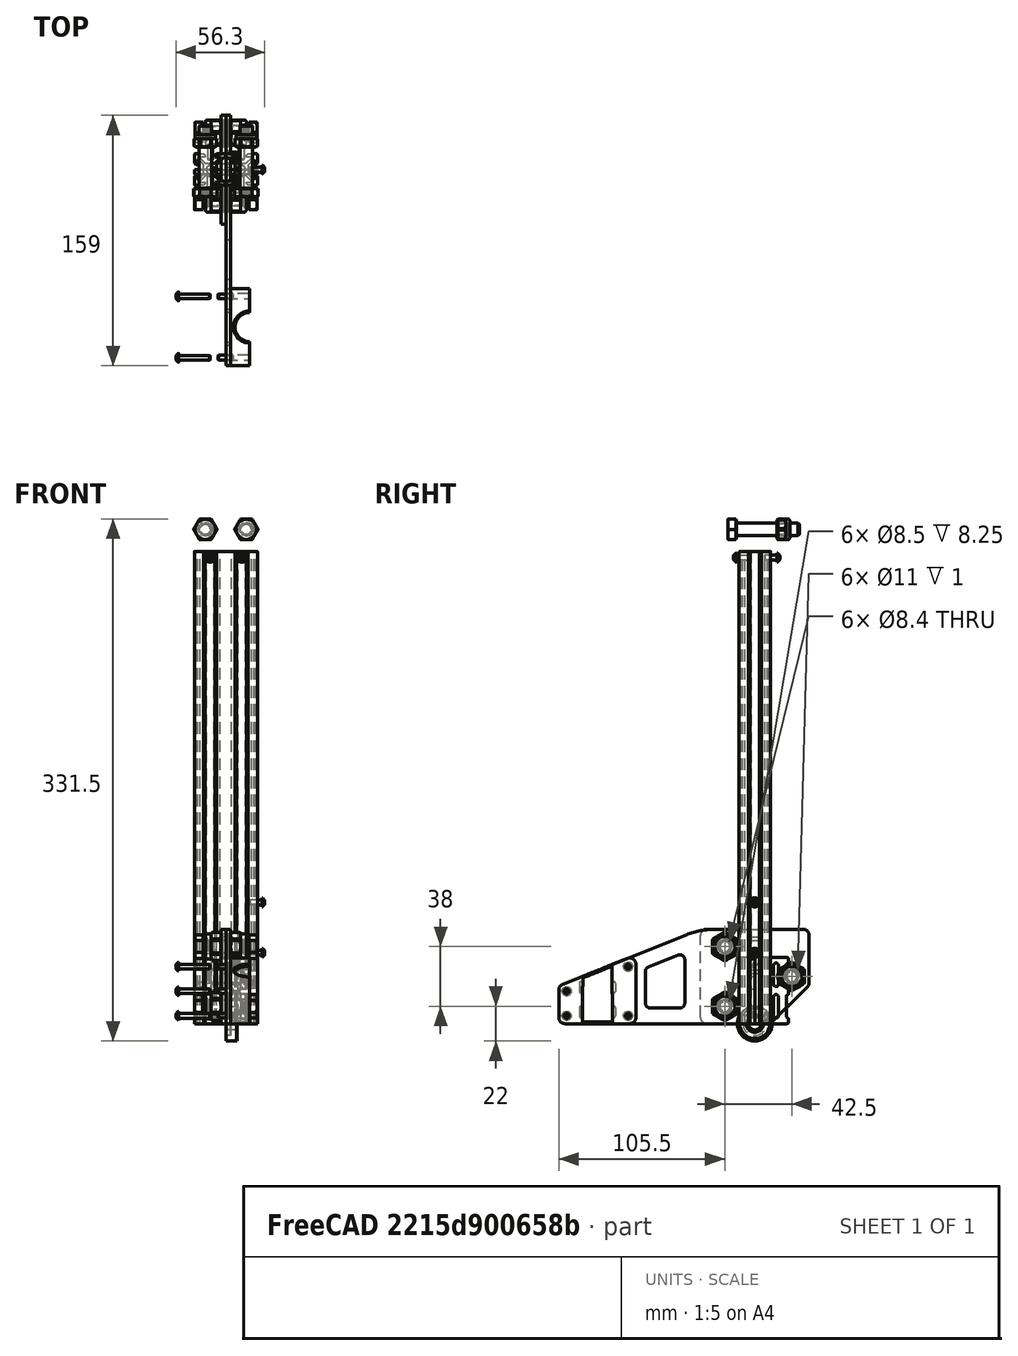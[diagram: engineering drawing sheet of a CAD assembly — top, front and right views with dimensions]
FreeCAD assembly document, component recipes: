
FREECAD ASSEMBLY — COMPONENT RECIPES ("BarbaHeatSetInsertPress")

This assembly document has 10 components, labeled P0..P9 below (a component is one placed body or linked part). 9 of them carry a construction recipe — the FreeCAD feature program that regenerates the part from scratch, quoted from this document or its linked companion documents; the rest are supplied as boundary geometry only. No exploded tour is included for this assembly.
COMPONENT P0 — recipe-attached ("PorteFer", modeled in this document).
Construction recipe (the document's own serialized feature program — sketch geometry with constraints, then the solid features built on it; lengths are millimeters unless a unit is written):

FEATURE [Sketcher::SketchObject] Sketch
  FullyConstrained = true
  MapMode = 5
  Placement = pos=(0,0,0) rot=(0.57735,0.57735,0.57735;2.0944rad)
  Support = -> [YZ_Plane]
  sketch-geometry (53):
    g0: LineSegment StartX=-124.5 StartY=0 StartZ=0 EndX=-124.5 EndY=24 EndZ=0
    g1: LineSegment StartX=-124.5 StartY=24 StartZ=0 EndX=-34.5 EndY=60 EndZ=0
    g2: LineSegment StartX=-34.5 StartY=60 StartZ=0 EndX=34.5 EndY=60 EndZ=0
    g3: LineSegment StartX=34.5 StartY=60 StartZ=0 EndX=34.5 EndY=24.5 EndZ=0
    g4: LineSegment StartX=34.5 StartY=24.5 StartZ=0 EndX=10 EndY=0 EndZ=0
    g5: LineSegment StartX=10 StartY=0 StartZ=0 EndX=-124.5 EndY=0 EndZ=0
    g6: LineSegment [constr] StartX=-109.5 StartY=0 StartZ=0 EndX=-109.5 EndY=30 EndZ=0
    g7: LineSegment [constr] StartX=-90.5 StartY=37.6 StartZ=0 EndX=-90.5 EndY=0 EndZ=0
    g8: LineSegment [constr] StartX=-100 StartY=0 StartZ=0 EndX=-100 EndY=33.8 EndZ=0
    g9: LineSegment [constr] StartX=10 StartY=0 StartZ=0 EndX=10 EndY=60 EndZ=0
    g10: LineSegment [constr] StartX=-10 StartY=60 StartZ=0 EndX=-10 EndY=0 EndZ=0
    g11: Circle [constr] CenterX=-19 CenterY=49 CenterZ=0 NormalX=0 NormalY=0 NormalZ=1 AngleXU=0 Radius=11
    g12: Circle [constr] CenterX=-19 CenterY=11 CenterZ=0 NormalX=0 NormalY=0 NormalZ=1 AngleXU=0 Radius=11
    g13: Circle CenterX=-19 CenterY=49 CenterZ=0 NormalX=0 NormalY=0 NormalZ=1 AngleXU=0 Radius=4.05
    g14: Circle CenterX=-19 CenterY=11 CenterZ=0 NormalX=0 NormalY=0 NormalZ=1 AngleXU=0 Radius=4.05
    g15: LineSegment [constr] StartX=-19 StartY=49 StartZ=0 EndX=-19 EndY=11 EndZ=0
    g16: LineSegment [constr] StartX=-19 StartY=30 StartZ=0 EndX=18.5 EndY=30 EndZ=0
    g17: ArcOfCircle CenterX=18.5 CenterY=30 CenterZ=0 NormalX=0 NormalY=0 NormalZ=1 AngleXU=0 Radius=4.05 StartAngle=1.5708 EndAngle=4.71239
    g18: ArcOfCircle CenterX=23.5 CenterY=30 CenterZ=0 NormalX=0 NormalY=0 NormalZ=1 AngleXU=0 Radius=4.05 StartAngle=4.71239 EndAngle=7.85398
    g19: LineSegment StartX=18.5 StartY=25.95 StartZ=0 EndX=23.5 EndY=25.95 EndZ=0
    g20: LineSegment StartX=18.5 StartY=34.05 StartZ=0 EndX=23.5 EndY=34.05 EndZ=0
    g21: LineSegment StartX=-69.5 StartY=10 StartZ=0 EndX=-69.5 EndY=35.2297 EndZ=0
    g22: LineSegment StartX=-69.5 StartY=35.2297 StartZ=0 EndX=-44.5 EndY=45.2297 EndZ=0
    g23: LineSegment StartX=-44.5 StartY=45.2297 StartZ=0 EndX=-44.5 EndY=10 EndZ=0
    g24: LineSegment StartX=-44.5 StartY=10 StartZ=0 EndX=-69.5 EndY=10 EndZ=0
    g25: Circle CenterX=-119.5 CenterY=20.6148 CenterZ=0 NormalX=0 NormalY=0 NormalZ=1 AngleXU=0 Radius=1.6
    g26: Circle CenterX=-119.5 CenterY=5 CenterZ=0 NormalX=0 NormalY=0 NormalZ=1 AngleXU=0 Radius=1.6
    g27: Circle CenterX=-80.5 CenterY=36.2148 CenterZ=0 NormalX=0 NormalY=0 NormalZ=1 AngleXU=0 Radius=1.6
    g28: Circle CenterX=-80.5 CenterY=5 CenterZ=0 NormalX=0 NormalY=0 NormalZ=1 AngleXU=0 Radius=1.6
    g29: ArcOfCircle CenterX=-110.5 CenterY=25.6148 CenterZ=0 NormalX=0 NormalY=0 NormalZ=1 AngleXU=0 Radius=1 StartAngle=1.9e-15 EndAngle=3.14159
    g30: ArcOfCircle CenterX=-110.5 CenterY=20.6148 CenterZ=0 NormalX=0 NormalY=0 NormalZ=1 AngleXU=0 Radius=1 StartAngle=3.14159 EndAngle=6.28319
    g31: LineSegment StartX=-111.5 StartY=25.6148 StartZ=0 EndX=-111.5 EndY=20.6148 EndZ=0
    g32: LineSegment StartX=-109.5 StartY=25.6148 StartZ=0 EndX=-109.5 EndY=20.6148 EndZ=0
    g33: ArcOfCircle CenterX=-110.5 CenterY=10 CenterZ=0 NormalX=0 NormalY=0 NormalZ=1 AngleXU=0 Radius=1 StartAngle=-9e-16 EndAngle=3.14159
    g34: ArcOfCircle CenterX=-110.5 CenterY=5 CenterZ=0 NormalX=0 NormalY=0 NormalZ=1 AngleXU=0 Radius=1 StartAngle=3.14159 EndAngle=6.28319
    g35: LineSegment StartX=-111.5 StartY=10 StartZ=0 EndX=-111.5 EndY=5 EndZ=0
    g36: LineSegment StartX=-109.5 StartY=10 StartZ=0 EndX=-109.5 EndY=5 EndZ=0
    g37: ArcOfCircle CenterX=-89.5 CenterY=25.6148 CenterZ=0 NormalX=0 NormalY=0 NormalZ=1 AngleXU=0 Radius=1 StartAngle=1e-15 EndAngle=3.14159
    g38: ArcOfCircle CenterX=-89.5 CenterY=20.6148 CenterZ=0 NormalX=0 NormalY=0 NormalZ=1 AngleXU=0 Radius=1 StartAngle=3.14159 EndAngle=6.28319
    g39: LineSegment StartX=-90.5 StartY=25.6148 StartZ=0 EndX=-90.5 EndY=20.6148 EndZ=0
    g40: LineSegment StartX=-88.5 StartY=25.6148 StartZ=0 EndX=-88.5 EndY=20.6148 EndZ=0
    g41: ArcOfCircle CenterX=-89.5 CenterY=10 CenterZ=0 NormalX=0 NormalY=0 NormalZ=1 AngleXU=0 Radius=1 StartAngle=-9e-16 EndAngle=3.14159
    g42: ArcOfCircle CenterX=-89.5 CenterY=5 CenterZ=0 NormalX=0 NormalY=0 NormalZ=1 AngleXU=0 Radius=1 StartAngle=3.14159 EndAngle=6.28319
    g43: LineSegment StartX=-90.5 StartY=10 StartZ=0 EndX=-90.5 EndY=5 EndZ=0
    g44: LineSegment StartX=-88.5 StartY=10 StartZ=0 EndX=-88.5 EndY=5 EndZ=0
    g45: LineSegment StartX=-3.5 StartY=55 StartZ=0 EndX=3.5 EndY=55 EndZ=0
    g46: LineSegment StartX=3.5 StartY=55 StartZ=0 EndX=3.5 EndY=52.5 EndZ=0
    g47: LineSegment StartX=3.5 StartY=52.5 StartZ=0 EndX=-3.5 EndY=52.5 EndZ=0
    g48: LineSegment StartX=-3.5 StartY=52.5 StartZ=0 EndX=-3.5 EndY=55 EndZ=0
    g49: LineSegment StartX=-3.5 StartY=44.5 StartZ=0 EndX=3.5 EndY=44.5 EndZ=0
    g50: LineSegment StartX=3.5 StartY=44.5 StartZ=0 EndX=3.5 EndY=42 EndZ=0
    g51: LineSegment StartX=3.5 StartY=42 StartZ=0 EndX=-3.5 EndY=42 EndZ=0
    g52: LineSegment StartX=-3.5 StartY=42 StartZ=0 EndX=-3.5 EndY=44.5 EndZ=0
  constraints (143):
    c: PointOnObject(g0,g-1)
    c: Vertical(g0)
    c: Coincident(g0,g1)
    c: Coincident(g1,g2)
    c: Coincident(g2,g3)
    c: Vertical(g3)
    c: Coincident(g3,g4)
    c: PointOnObject(g4,g-1)
    c: Coincident(g4,g5)
    c: Coincident(g5,g0)
    c: DistanceX(g-1,g4) = 10
    c: PointOnObject(g6,g5)
    c: PointOnObject(g6,g1)
    c: Vertical(g6)
    c: PointOnObject(g7,g1)
    c: PointOnObject(g7,g5)
    c: Vertical(g7)
    c: DistanceX(g6,g7) = 19
    c: PointOnObject(g8,g1)
    c: Vertical(g8)
    c: Symmetric(g6,g7,g8)
    c: DistanceX(g8,g-1) = 100
    c: DistanceX(g0,g6) = 15
    c: Symmetric(g2,g1,g-2)
    c: Angle(g4,g5) = 2.35619
    c: Coincident(g9,g4)
    c: PointOnObject(g9,g2)
    c: Vertical(g9)
    c: PointOnObject(g10,g5)
    c: Vertical(g10)
    c: Symmetric(g10,g9,g-2)
    c: Diameter(g11) = 22
    c: Equal(g11,g12)
    c: DistanceX(g11,g10) = 9
    c: Vertical(g12,g11)
    c: Coincident(g13,g11)
    c: Coincident(g14,g12)
    c: Diameter(g13) = 8.1
    c: Equal(g13,g14)
    c: Coincident(g15,g13)
    c: Coincident(g15,g14)
    c: Symmetric(g14,g13,g16)
    c: DistanceX(g9,g16) = 8.5
    c: Tangent(g17,g20) = 1.5708
    c: Tangent(g17,g19) = -1.5708
    c: Tangent(g19,g18) = -1.5708
    c: Tangent(g20,g18) = 1.5708
    c: Horizontal(g19)
    c: Equal(g17,g18)
    c: Coincident(g17,g16)
    c: Equal(g17,g13)
    c: DistanceX(g17,g18) = 5
    c: DistanceY(g13,g10) = 11
    c: Symmetric(g10,g10,g16)
    c: DistanceX(g18,g3) = 11
    c: DistanceY(g6,g6) = 30
    c: DistanceY(g1) = 60
    c: Vertical(g21)
    c: Coincident(g21,g22)
    c: Coincident(g22,g23)
    c: Vertical(g23)
    c: Coincident(g23,g24)
    c: Coincident(g24,g21)
    c: Horizontal(g24)
    c: DistanceY(g23) = 10
    c: Parallel(g22,g1)
    c: Distance(g22,g1) = 10
    c: DistanceX(g22,g1) = 10
    c: DistanceX(g24,g24) = 25
    c: Equal(g25,g26)
    c: Equal(g26,g27)
    c: Equal(g27,g28)
    c: Diameter(g27) = 3.2
    c: Vertical(g26,g25)
    c: Vertical(g28,g27)
    c: DistanceX(g0,g25) = 5
    c: DistanceY(g0,g26) = 5
    c: Distance(g25,g1) = 5
    c: Distance(g27,g1) = 5
    c: Symmetric(g26,g28,g8)
    c: Tangent(g29,g32) = 1.5708
    c: Tangent(g29,g31) = -1.5708
    c: Tangent(g31,g30) = -1.5708
    c: Tangent(g32,g30) = 1.5708
    c: Vertical(g31)
    c: Equal(g29,g30)
    c: Tangent(g33,g36) = 1.5708
    c: Tangent(g33,g35) = -1.5708
    c: Tangent(g35,g34) = -1.5708
    c: Tangent(g36,g34) = 1.5708
    c: Vertical(g35)
    c: Equal(g33,g34)
    c: Tangent(g37,g40) = 1.5708
    c: Tangent(g37,g39) = -1.5708
    c: Tangent(g39,g38) = -1.5708
    c: Tangent(g40,g38) = 1.5708
    c: Vertical(g39)
    c: Equal(g37,g38)
    c: Tangent(g41,g44) = 1.5708
    c: Tangent(g41,g43) = -1.5708
    c: Tangent(g43,g42) = -1.5708
    c: Tangent(g44,g42) = 1.5708
    c: Vertical(g43)
    c: Equal(g41,g42)
    c: Horizontal(g34,g42)
    c: Horizontal(g29,g37)
    c: Equal(g30,g38)
    c: Equal(g38,g41)
    c: Equal(g41,g33)
    c: PointOnObject(g41,g7)
    c: PointOnObject(g37,g7)
    c: PointOnObject(g29,g6)
    c: PointOnObject(g33,g6)
    c: Equal(g36,g32)
    c: Equal(g32,g39)
    c: Equal(g39,g43)
    c: DistanceY(g30,g29) = 5
    c: Horizontal(g34,g26)
    c: Horizontal(g30,g25)
    c: Diameter(g29) = 2
    c: Coincident(g45,g46)
    c: Coincident(g46,g47)
    c: Coincident(g47,g48)
    c: Coincident(g48,g45)
    c: Horizontal(g45)
    c: Horizontal(g47)
    c: Vertical(g46)
    c: Vertical(g48)
    c: Coincident(g49,g50)
    c: Coincident(g50,g51)
    c: Coincident(g51,g52)
    c: Coincident(g52,g49)
    c: Horizontal(g51)
    c: Vertical(g50)
    c: Vertical(g52)
    c: Symmetric(g49,g49,g-2)
    c: Vertical(g49,g46)
    c: Equal(g50,g46)
    c: DistanceX(g45,g45) = 7
    c: Vertical(g49,g47)
    c: DistanceY(g46,g46) = 2.5
    c: DistanceY(g45,g2) = 5
    c: DistanceY(g49,g46) = 8
FEATURE [PartDesign::Pad] Pad
  AddSubType = 0
  CheckUpToFaceLimits = true
  ClaimChildren = false
  Direction = (1,1,1)
  Fit = 0
  FitJoin = 0
  InnerFit = 0
  InnerFitJoin = 0
  InnerTaperAngle = 0
  InnerTaperAngleRev = 0
  Length = 3
  Length2 = 100
  Linearize = true
  NewSolid = false
  Placement = pos=(0,0,0) rot=(0.57735,0.57735,0.57735;2.0944rad)
  Profile = -> Sketch
  Refine = true
  Suppress = false
  Type = 0
  _ProfileBasedVersion = 1
FEATURE [PartDesign::Fillet] Fillet
  AddSubType = 0
  Base = -> Pad [Edge8,Edge2,Edge1]
  BaseFeature = -> Pad
  NewSolid = false
  Placement = pos=(0,0,0) rot=(0.57735,0.57735,0.57735;2.0944rad)
  Radius = 4
  Refine = true
  SupportTransform = false
  Suppress = false
FEATURE [PartDesign::Fillet] Fillet001
  AddSubType = 0
  Base = -> Fillet [Edge101,Edge99]
  BaseFeature = -> Fillet
  NewSolid = false
  Placement = pos=(0,0,0) rot=(0.57735,0.57735,0.57735;2.0944rad)
  Radius = 3
  Refine = true
  SupportTransform = false
  Suppress = false
FEATURE [PartDesign::Fillet] Fillet002
  AddSubType = 0
  Base = -> Fillet001 [Edge67]
  BaseFeature = -> Fillet001
  NewSolid = false
  Placement = pos=(0,0,0) rot=(0.57735,0.57735,0.57735;2.0944rad)
  Radius = 50
  Refine = true
  SupportTransform = false
  Suppress = false
FEATURE [PartDesign::Fillet] Fillet003
  AddSubType = 0
  Base = -> Fillet002 [Edge78,Edge80,Edge75,Edge76]
  BaseFeature = -> Fillet002
  NewSolid = false
  Placement = pos=(0,0,0) rot=(0.57735,0.57735,0.57735;2.0944rad)
  Radius = 3
  Refine = true
  SupportTransform = false
  Suppress = false
FEATURE [PartDesign::Body] Body  label="PorteFer"
  AutoGroupSolids = false
  ExportMode = 0
  Group = -> [Sketch,Pad,Fillet,Fillet001,Fillet002,Fillet003]
  Origin = -> Origin
  SingleSolid = true
  Tip = -> Fillet003
  _ExportChildren = -> [Pad,Fillet,Fillet001,Fillet002,Fillet003]
  _GroupVersion = 1
COMPONENT P1 — recipe-attached ("Rondelle", modeled in this document).
Construction recipe (the document's own serialized feature program — sketch geometry with constraints, then the solid features built on it; lengths are millimeters unless a unit is written):

FEATURE [Sketcher::SketchObject] Sketch001
  FullyConstrained = true
  MapMode = 5
  Placement = pos=(0,0,0) rot=(0.57735,0.57735,0.57735;2.0944rad)
  Support = -> [YZ_Plane001]
  sketch-geometry (2):
    g0: Circle CenterX=0 CenterY=0 CenterZ=0 NormalX=0 NormalY=0 NormalZ=1 AngleXU=0 Radius=4
    g1: Circle CenterX=0 CenterY=0 CenterZ=0 NormalX=0 NormalY=0 NormalZ=1 AngleXU=0 Radius=7.5
  constraints (4):
    c: Coincident(g0,g-1)
    c: Coincident(g1,g0)
    c: Diameter(g0) = 8
    c: Diameter(g1) = 15
FEATURE [PartDesign::Pad] Pad001
  AddSubType = 0
  CheckUpToFaceLimits = true
  ClaimChildren = false
  Direction = (1,1,1)
  Fit = 0
  FitJoin = 0
  InnerFit = 0
  InnerFitJoin = 0
  InnerTaperAngle = 0
  InnerTaperAngleRev = 0
  Length = 3
  Length2 = 100
  Linearize = true
  NewSolid = false
  Placement = pos=(0,0,0) rot=(0.57735,0.57735,0.57735;2.0944rad)
  Profile = -> Sketch001
  Refine = true
  Suppress = false
  Type = 0
  _ProfileBasedVersion = 1
FEATURE [PartDesign::Body] Body001  label="Rondelle"
  AutoGroupSolids = false
  ExportMode = 0
  Group = -> [Sketch001,Pad001]
  Origin = -> Origin001
  SingleSolid = true
  Tip = -> Pad001
  _ExportChildren = -> [Pad001]
  _GroupVersion = 1
COMPONENT P2 — recipe-attached ("Chariot", modeled in this document).
Construction recipe (the document's own serialized feature program — sketch geometry with constraints, then the solid features built on it; lengths are millimeters unless a unit is written):

FEATURE [PartDesign::SubShapeBinder] Binder  label="Binder(Fillet003)"
  BindCopyOnChange = 0
  BindMode = 0
  ClaimChildren = false
  Context = -> Body002 [Binder.]
  FillStyle = 0
  Fuse = false
  MakeFace = true
  PartialLoad = false
  Relative = true
  Support = -> [Body[Fillet003.Face1]]
  _Version = 8
FEATURE [Sketcher::SketchObject] Sketch002
  ExternalGeometry = -> [Binder]
  FullyConstrained = true
  MapMode = 5
  Placement = pos=(0,0,0) rot=(0.57735,0.57735,0.57735;2.0944rad)
  Support = -> [YZ_Plane002]
  sketch-geometry (8):
    g0: LineSegment StartX=8.75736 StartY=0 StartZ=0 EndX=-34.5 EndY=0 EndZ=0
    g1: LineSegment StartX=-34.5 StartY=0 StartZ=0 EndX=-34.5 EndY=60 EndZ=0
    g2: LineSegment StartX=-34.5 StartY=60 StartZ=0 EndX=30.5 EndY=60 EndZ=0
    g3: GeomPoint [constr] X=-34.5 Y=56 Z=0
    g4: LineSegment StartX=-3.5 StartY=34 StartZ=0 EndX=3.5 EndY=34 EndZ=0
    g5: LineSegment StartX=3.5 StartY=34 StartZ=0 EndX=3.5 EndY=31.5 EndZ=0
    g6: LineSegment StartX=3.5 StartY=31.5 StartZ=0 EndX=-3.5 EndY=31.5 EndZ=0
    g7: LineSegment StartX=-3.5 StartY=31.5 StartZ=0 EndX=-3.5 EndY=34 EndZ=0
  constraints (19):
    c: Coincident(g0,g-21)
    c: PointOnObject(g0,g-1)
    c: Coincident(g1,g0)
    c: Coincident(g2,g1)
    c: Coincident(g2,g-18)
    c: Horizontal(g2)
    c: PointOnObject(g3,g1)
    c: Symmetric(g3,g-18,g-2)
    c: Vertical(g1)
    c: Coincident(g4,g5)
    c: Coincident(g5,g6)
    c: Coincident(g6,g7)
    c: Coincident(g7,g4)
    c: Horizontal(g6)
    c: Vertical(g5)
    c: Vertical(g7)
    c: Equal(g5,g-12)
    c: Symmetric(g4,g4,g-2)
    c: Symmetric(g4,g-16,g-12)
FEATURE [PartDesign::Pad] Pad002
  AddSubType = 0
  CheckUpToFaceLimits = true
  ClaimChildren = false
  Direction = (1,1,1)
  Fit = 0
  FitJoin = 0
  InnerFit = 0
  InnerFitJoin = 0
  InnerTaperAngle = 0
  InnerTaperAngleRev = 0
  Length = 3
  Length2 = 100
  Linearize = true
  NewSolid = false
  Placement = pos=(0,0,0) rot=(0.57735,0.57735,0.57735;2.0944rad)
  Profile = -> Sketch002
  Refine = true
  Reversed = true
  Suppress = false
  Type = 0
  _ProfileBasedVersion = 1
FEATURE [PartDesign::Fillet] Fillet004
  AddSubType = 0
  Base = -> Pad002 [Edge5,Edge2]
  BaseFeature = -> Pad002
  NewSolid = false
  Placement = pos=(0,0,0) rot=(0.57735,0.57735,0.57735;2.0944rad)
  Radius = 4
  Refine = true
  SupportTransform = false
  Suppress = false
FEATURE [PartDesign::Body] Body002  label="Chariot"
  AutoGroupSolids = false
  ExportMode = 0
  Group = -> [Binder,Sketch002,Pad002,Fillet004]
  Origin = -> Origin002
  SingleSolid = true
  Tip = -> Fillet004
  _ExportChildren = -> [Binder,Pad002,Fillet004]
  _GroupVersion = 1
COMPONENT P3 — recipe-attached ("RenvoiAngle", modeled in this document).
Construction recipe (the document's own serialized feature program — sketch geometry with constraints, then the solid features built on it; lengths are millimeters unless a unit is written):

FEATURE [Sketcher::SketchObject] Sketch003
  FullyConstrained = true
  MapMode = 5
  Placement = pos=(0,0,0) rot=(1,0,0;1.5708rad)
  Support = -> [XZ_Plane003]
  sketch-geometry (11):
    g0: LineSegment StartX=-20 StartY=0 StartZ=0 EndX=20 EndY=0 EndZ=0
    g1: LineSegment StartX=20 StartY=0 StartZ=0 EndX=20 EndY=41 EndZ=0
    g2: LineSegment StartX=20 StartY=41 StartZ=0 EndX=-20 EndY=41 EndZ=0
    g3: LineSegment StartX=-20 StartY=41 StartZ=0 EndX=-20 EndY=0 EndZ=0
    g4: Circle CenterX=-13 CenterY=26 CenterZ=0 NormalX=0 NormalY=0 NormalZ=1 AngleXU=0 Radius=4
    g5: Circle CenterX=13 CenterY=26 CenterZ=0 NormalX=0 NormalY=0 NormalZ=1 AngleXU=0 Radius=4
    g6: Circle [constr] CenterX=13 CenterY=26 CenterZ=0 NormalX=0 NormalY=0 NormalZ=1 AngleXU=0 Radius=11
    g7: Circle [constr] CenterX=-13 CenterY=26 CenterZ=0 NormalX=0 NormalY=0 NormalZ=1 AngleXU=0 Radius=11
    g8: Circle CenterX=-10 CenterY=8 CenterZ=0 NormalX=0 NormalY=0 NormalZ=1 AngleXU=0 Radius=1.5
    g9: Circle CenterX=10 CenterY=8 CenterZ=0 NormalX=0 NormalY=0 NormalZ=1 AngleXU=0 Radius=1.5
    g10: GeomPoint [constr] X=24 Y=26 Z=0
  constraints (27):
    c: Coincident(g0,g1)
    c: Coincident(g1,g2)
    c: Coincident(g2,g3)
    c: Coincident(g3,g0)
    c: Horizontal(g0)
    c: Vertical(g1)
    c: Vertical(g3)
    c: PointOnObject(g0,g-1)
    c: Symmetric(g1,g2,g-2)
    c: Symmetric(g5,g4,g-2)
    c: Diameter(g4) = 8
    c: Equal(g4,g5)
    c: Coincident(g6,g5)
    c: Coincident(g7,g4)
    c: Diameter(g6) = 22
    c: Equal(g6,g7)
    c: DistanceX(g2,g1) = 40
    c: DistanceY(g5,g1) = 15
    c: Diameter(g8) = 3
    c: Equal(g9,g8)
    c: Symmetric(g9,g8,g-2)
    c: DistanceX(g-1,g9) = 10
    c: DistanceY(g-1,g9) = 8
    c: DistanceY(g9,g5) = 18
    c: PointOnObject(g10,g6)
    c: Horizontal(g10,g5)
    c: DistanceX(g0,g10) = 4
FEATURE [PartDesign::Pad] Pad003
  AddSubType = 0
  CheckUpToFaceLimits = true
  ClaimChildren = false
  Direction = (1,1,1)
  Fit = 0
  FitJoin = 0
  InnerFit = 0
  InnerFitJoin = 0
  InnerTaperAngle = 0
  InnerTaperAngleRev = 0
  Length = 3
  Length2 = 100
  Linearize = true
  NewSolid = false
  Placement = pos=(0,0,0) rot=(1,0,0;1.5708rad)
  Profile = -> Sketch003
  Refine = true
  Suppress = false
  Type = 0
  _ProfileBasedVersion = 1
FEATURE [PartDesign::Fillet] Fillet005
  AddSubType = 0
  Base = -> Pad003 [Edge5,Edge8,Edge1,Edge2]
  BaseFeature = -> Pad003
  NewSolid = false
  Placement = pos=(0,0,0) rot=(1,0,0;1.5708rad)
  Radius = 4
  Refine = true
  SupportTransform = false
  Suppress = false
FEATURE [PartDesign::Body] Body003  label="RenvoiAngle"
  AutoGroupSolids = false
  ExportMode = 0
  Group = -> [Sketch003,Pad003,Fillet005]
  Origin = -> Origin003
  SingleSolid = true
  Tip = -> Fillet005
  _ExportChildren = -> [Pad003,Fillet005]
  _GroupVersion = 1
COMPONENT P4 — recipe-attached ("GuideCable", modeled in this document).
Construction recipe (the document's own serialized feature program — sketch geometry with constraints, then the solid features built on it; lengths are millimeters unless a unit is written):

FEATURE [Sketcher::SketchObject] Sketch004
  FullyConstrained = true
  MapMode = 5
  Placement = pos=(0,0,0) rot=(0.57735,0.57735,0.57735;2.0944rad)
  Support = -> [YZ_Plane004]
  sketch-geometry (29):
    g0: LineSegment StartX=-10 StartY=0 StartZ=0 EndX=21.5 EndY=0 EndZ=0
    g1: LineSegment [constr] StartX=21.5 StartY=0 StartZ=0 EndX=21.5 EndY=42 EndZ=0
    g2: LineSegment StartX=21.5 StartY=42 StartZ=0 EndX=-10 EndY=42 EndZ=0
    g3: LineSegment StartX=-10 StartY=42 StartZ=0 EndX=-10 EndY=0 EndZ=0
    g4: Circle CenterX=0 CenterY=37 CenterZ=0 NormalX=0 NormalY=0 NormalZ=1 AngleXU=0 Radius=1.6
    g5: Circle CenterX=0 CenterY=5 CenterZ=0 NormalX=0 NormalY=0 NormalZ=1 AngleXU=0 Radius=1.6
    g6: ArcOfCircle CenterX=13.5 CenterY=37 CenterZ=0 NormalX=0 NormalY=0 NormalZ=1 AngleXU=0 Radius=1.5 StartAngle=2e-15 EndAngle=3.14159
    g7: ArcOfCircle CenterX=13.5 CenterY=25 CenterZ=0 NormalX=0 NormalY=0 NormalZ=1 AngleXU=0 Radius=1.5 StartAngle=3.14159 EndAngle=6.28319
    g8: LineSegment StartX=12 StartY=37 StartZ=0 EndX=12 EndY=25 EndZ=0
    g9: LineSegment StartX=15 StartY=37 StartZ=0 EndX=15 EndY=25 EndZ=0
    g10: ArcOfCircle CenterX=13.5 CenterY=17 CenterZ=0 NormalX=0 NormalY=0 NormalZ=1 AngleXU=0 Radius=1.5 StartAngle=1.1e-15 EndAngle=3.14159
    g11: ArcOfCircle CenterX=13.5 CenterY=5 CenterZ=0 NormalX=0 NormalY=0 NormalZ=1 AngleXU=0 Radius=1.5 StartAngle=3.14159 EndAngle=6.28319
    g12: LineSegment StartX=12 StartY=17 StartZ=0 EndX=12 EndY=5 EndZ=0
    g13: LineSegment StartX=15 StartY=17 StartZ=0 EndX=15 EndY=5 EndZ=0
    g14: ArcOfCircle [constr] CenterX=21.5 CenterY=37 CenterZ=0 NormalX=0 NormalY=0 NormalZ=1 AngleXU=0 Radius=1.5 StartAngle=2e-15 EndAngle=3.14159
    g15: ArcOfCircle [constr] CenterX=21.5 CenterY=25 CenterZ=0 NormalX=0 NormalY=0 NormalZ=1 AngleXU=0 Radius=1.5 StartAngle=3.14159 EndAngle=6.28319
    g16: LineSegment StartX=20 StartY=37 StartZ=0 EndX=20 EndY=25 EndZ=0
    g17: LineSegment [constr] StartX=23 StartY=37 StartZ=0 EndX=23 EndY=25 EndZ=0
    g18: ArcOfCircle [constr] CenterX=21.5 CenterY=17 CenterZ=0 NormalX=0 NormalY=0 NormalZ=1 AngleXU=0 Radius=1.5 StartAngle=-9e-16 EndAngle=3.14159
    g19: ArcOfCircle [constr] CenterX=21.5 CenterY=5 CenterZ=0 NormalX=0 NormalY=0 NormalZ=1 AngleXU=0 Radius=1.5 StartAngle=3.14159 EndAngle=6.28319
    g20: LineSegment StartX=20 StartY=17 StartZ=0 EndX=20 EndY=5 EndZ=0
    g21: LineSegment [constr] StartX=23 StartY=17 StartZ=0 EndX=23 EndY=5 EndZ=0
    g22: LineSegment StartX=21.5 StartY=42 StartZ=0 EndX=21.5 EndY=38.5 EndZ=0
    g23: LineSegment StartX=21.5 StartY=23.5 StartZ=0 EndX=21.5 EndY=18.5 EndZ=0
    g24: LineSegment StartX=21.5 StartY=0 StartZ=0 EndX=21.5 EndY=3.5 EndZ=0
    g25: ArcOfCircle CenterX=21.5 CenterY=25 CenterZ=0 NormalX=0 NormalY=0 NormalZ=1 AngleXU=0 Radius=1.5 StartAngle=3.14159 EndAngle=4.71239
    g26: ArcOfCircle CenterX=21.5 CenterY=17 CenterZ=0 NormalX=0 NormalY=0 NormalZ=1 AngleXU=0 Radius=1.5 StartAngle=1.5708 EndAngle=3.14159
    g27: ArcOfCircle CenterX=21.5 CenterY=5 CenterZ=0 NormalX=0 NormalY=0 NormalZ=1 AngleXU=0 Radius=1.5 StartAngle=3.14159 EndAngle=4.71239
    g28: ArcOfCircle CenterX=21.5 CenterY=37 CenterZ=0 NormalX=0 NormalY=0 NormalZ=1 AngleXU=0 Radius=1.5 StartAngle=1.5708 EndAngle=3.14159
  constraints (76):
    c: Coincident(g0,g1)
    c: Coincident(g1,g2)
    c: Coincident(g2,g3)
    c: Coincident(g3,g0)
    c: Horizontal(g0)
    c: Horizontal(g2)
    c: Vertical(g1)
    c: Vertical(g3)
    c: PointOnObject(g0,g-1)
    c: DistanceX(g0) = -10
    c: PointOnObject(g4,g-2)
    c: PointOnObject(g5,g-2)
    c: Diameter(g5) = 3.2
    c: Equal(g5,g4)
    c: DistanceY(g4,g2) = 5
    c: DistanceY(g0,g5) = 5
    c: Tangent(g6,g9) = 1.5708
    c: Tangent(g6,g8) = -1.5708
    c: Tangent(g8,g7) = -1.5708
    c: Tangent(g9,g7) = 1.5708
    c: Vertical(g8)
    c: Equal(g6,g7)
    c: Tangent(g10,g13) = 1.5708
    c: Tangent(g10,g12) = -1.5708
    c: Tangent(g12,g11) = -1.5708
    c: Tangent(g13,g11) = 1.5708
    c: Vertical(g12)
    c: Equal(g10,g11)
    c: Tangent(g14,g17) = 1.5708
    c: Tangent(g14,g16) = -1.5708
    c: Tangent(g16,g15) = -1.5708
    c: Tangent(g17,g15) = 1.5708
    c: Vertical(g16)
    c: Equal(g14,g15)
    c: PointOnObject(g14,g1)
    c: Tangent(g18,g21) = 1.5708
    c: Tangent(g18,g20) = -1.5708
    c: Tangent(g20,g19) = -1.5708
    c: Tangent(g21,g19) = 1.5708
    c: Vertical(g20)
    c: Equal(g18,g19)
    c: PointOnObject(g18,g1)
    c: Horizontal(g10,g18)
    c: Horizontal(g19,g11)
    c: Horizontal(g7,g15)
    c: Horizontal(g6,g14)
    c: Equal(g6,g14)
    c: Equal(g14,g10)
    c: Equal(g10,g18)
    c: Diameter(g14) = 3
    c: Equal(g17,g21)
    c: Horizontal(g6,g4)
    c: Horizontal(g11,g5)
    c: DistanceY(g17,g17) = 12
    c: DistanceY(g10,g7) = 8
    c: Vertical(g7,g10)
    c: DistanceX(g6,g14) = 5
    c: Coincident(g22,g2)
    c: PointOnObject(g22,g1)
    c: PointOnObject(g23,g1)
    c: PointOnObject(g23,g1)
    c: Coincident(g24,g0)
    c: Vertical(g24)
    c: DistanceX(g6) = 12
    c: Coincident(g25,g15)
    c: Coincident(g25,g16)
    c: Coincident(g25,g23)
    c: Coincident(g26,g18)
    c: Coincident(g26,g23)
    c: Coincident(g26,g20)
    c: Coincident(g27,g19)
    c: Coincident(g27,g20)
    c: Coincident(g27,g24)
    c: Coincident(g28,g14)
    c: Coincident(g28,g16)
    c: Coincident(g28,g22)
FEATURE [PartDesign::Pad] Pad004
  AddSubType = 0
  CheckUpToFaceLimits = true
  ClaimChildren = false
  Direction = (1,1,1)
  Fit = 0
  FitJoin = 0
  InnerFit = 0
  InnerFitJoin = 0
  InnerTaperAngle = 0
  InnerTaperAngleRev = 0
  Length = 3
  Length2 = 100
  Linearize = true
  NewSolid = false
  Placement = pos=(0,0,0) rot=(0.57735,0.57735,0.57735;2.0944rad)
  Profile = -> Sketch004
  Refine = true
  Suppress = false
  Type = 0
  _ProfileBasedVersion = 1
FEATURE [PartDesign::Fillet] Fillet006
  AddSubType = 0
  Base = -> Pad004 [Edge2,Edge5,Edge8,Edge11,Edge20,Edge23,Edge32,Edge1]
  BaseFeature = -> Pad004
  NewSolid = false
  Placement = pos=(0,0,0) rot=(0.57735,0.57735,0.57735;2.0944rad)
  Radius = 1
  Refine = true
  SupportTransform = false
  Suppress = false
FEATURE [PartDesign::Body] Body004  label="GuideCable"
  AutoGroupSolids = false
  ExportMode = 0
  Group = -> [Sketch004,Pad004,Fillet006]
  Origin = -> Origin004
  SingleSolid = true
  Tip = -> Fillet006
  _ExportChildren = -> [Pad004,Fillet006]
  _GroupVersion = 1
COMPONENT P5 — recipe-attached ("MorsDroit", modeled in this document).
Construction recipe (the document's own serialized feature program — sketch geometry with constraints, then the solid features built on it; lengths are millimeters unless a unit is written):

FEATURE [PartDesign::SubShapeBinder] Binder001  label="Binder001(Fillet003)"
  BindCopyOnChange = 0
  BindMode = 0
  ClaimChildren = false
  Context = -> Body005 [Binder001.]
  FillStyle = 0
  Fuse = false
  MakeFace = true
  PartialLoad = false
  Relative = true
  Support = -> [Body[Fillet003.Face1]]
  _Version = 8
FEATURE [Part::SubShapeBinder] Import  label="Import(Fillet003)"
  BindCopyOnChange = 0
  BindMode = 0
  ClaimChildren = false
  Context = -> Body005 [Import.]
  FillStyle = 0
  Fuse = false
  MakeFace = false
  PartialLoad = false
  Relative = true
  Support = -> [Body[Fillet003.]]
  _Version = 8
FEATURE [Sketcher::SketchObject] Sketch005
  ExternalGeometry = -> [Import,Binder001]
  FullyConstrained = true
  MapMode = 5
  Placement = pos=(0,0,0) rot=(-0.57735,0.57735,0.57735;4.18879rad)
  Support = -> [YZ_Plane005]
  sketch-geometry (9):
    g0: LineSegment [constr] StartX=100 StartY=33.8 StartZ=0 EndX=100 EndY=-2.84e-14 EndZ=0
    g1: Circle CenterX=80.5 CenterY=36.2148 CenterZ=0 NormalX=0 NormalY=0 NormalZ=1 AngleXU=0 Radius=1.6
    g2: Circle CenterX=80.5 CenterY=5 CenterZ=0 NormalX=0 NormalY=0 NormalZ=1 AngleXU=0 Radius=1.6
    g3: Circle CenterX=119.5 CenterY=5 CenterZ=0 NormalX=0 NormalY=0 NormalZ=1 AngleXU=0 Radius=1.6
    g4: Circle CenterX=119.5 CenterY=20.6148 CenterZ=0 NormalX=0 NormalY=0 NormalZ=1 AngleXU=0 Radius=1.6
    g5: LineSegment StartX=75.5 StartY=43.6 StartZ=0 EndX=75.5 EndY=-2.13e-14 EndZ=0
    g6: GeomPoint [constr] X=75.5 Y=4 Z=0
    g7: LineSegment StartX=75.5 StartY=43.6 StartZ=0 EndX=121.986 EndY=25.0058 EndZ=0
    g8: LineSegment StartX=120.5 StartY=0 StartZ=0 EndX=75.5 EndY=-2.13e-14 EndZ=0
  constraints (20):
    c: PointOnObject(g0,g-9)
    c: PointOnObject(g0,g-10)
    c: Symmetric(g-4,g-6,g0)
    c: Coincident(g1,g-3)
    c: Coincident(g2,g-4)
    c: Coincident(g3,g-6)
    c: Coincident(g4,g-5)
    c: Diameter(g1) = 3.2
    c: Equal(g1,g2)
    c: Equal(g1,g4)
    c: Equal(g1,g3)
    c: PointOnObject(g5,g-9)
    c: PointOnObject(g5,g-10)
    c: Vertical(g5)
    c: PointOnObject(g6,g5)
    c: Symmetric(g6,g-11,g0)
    c: Coincident(g7,g5)
    c: Coincident(g7,g-9)
    c: Coincident(g8,g-11)
    c: Coincident(g8,g5)
FEATURE [PartDesign::Pad] Pad005
  AddSubType = 0
  CheckUpToFaceLimits = true
  ClaimChildren = false
  Direction = (1,1,1)
  Fit = 0
  FitJoin = 0
  InnerFit = 0
  InnerFitJoin = 0
  InnerTaperAngle = 0
  InnerTaperAngleRev = 0
  Length = 15
  Length2 = 100
  Linearize = true
  NewSolid = false
  Placement = pos=(0,0,0) rot=(0.57735,0.57735,0.57735;2.0944rad)
  Profile = -> Sketch005
  Refine = true
  Suppress = false
  Type = 0
  _ProfileBasedVersion = 1
FEATURE [Sketcher::SketchObject] Sketch006
  ExternalGeometry = -> [Pad005]
  FullyConstrained = true
  MapMode = 5
  Placement = pos=(-15,5.6e-15,-3.5e-15) rot=(-0.57735,-0.57735,0.57735;2.0944rad)
  Support = -> [Pad005]
  sketch-geometry (6):
    g0: LineSegment StartX=-100 StartY=0 StartZ=0 EndX=-100 EndY=-33.8 EndZ=0
    g1: GeomPoint [constr] X=-75.5 Y=-4 Z=0
    g2: LineSegment StartX=-100 StartY=0 StartZ=0 EndX=-90.5 EndY=0 EndZ=0
    g3: LineSegment StartX=-90.5 StartY=0 StartZ=0 EndX=-90.8512 EndY=-37.4595 EndZ=0
    g4: LineSegment StartX=-90.8512 StartY=-37.4595 StartZ=0 EndX=-100 EndY=-33.8 EndZ=0
    g5: LineSegment [constr] StartX=-100 StartY=-32 StartZ=0 EndX=-90.8 EndY=-32 EndZ=0
  constraints (17):
    c: PointOnObject(g0,g-1)
    c: Vertical(g0)
    c: PointOnObject(g0,g-3)
    c: PointOnObject(g1,g-5)
    c: Symmetric(g-4,g1,g0)
    c: Coincident(g2,g0)
    c: PointOnObject(g2,g-1)
    c: Coincident(g3,g2)
    c: PointOnObject(g3,g-3)
    c: Coincident(g4,g3)
    c: Coincident(g4,g0)
    c: DistanceX(g2,g2) = 9.5
    c: PointOnObject(g5,g0)
    c: PointOnObject(g5,g3)
    c: Horizontal(g5)
    c: DistanceY(g5,g0) = 32
    c: DistanceX(g5,g5) = 9.2
FEATURE [PartDesign::Line] DatumLine
  AttacherType = Attacher::AttachEngineLine
  Length = 60
  MapMode = 29
  MinimumLength = 10
  Placement = pos=(-15,-100,-3.5e-15) rot=(0,0,1;0rad)
  ResizeMode = 0
  Support = -> [Sketch006]
FEATURE [PartDesign::Groove] Groove
  AddSubType = 1
  Angle = 360
  Axis = (-4e-16,0,1)
  Base = (-15,-100,-5.1e-15)
  BaseFeature = -> Pad005
  ClaimChildren = false
  Fit = 0
  FitJoin = 0
  InnerFit = 0
  InnerFitJoin = 0
  NewSolid = false
  Placement = pos=(0,0,0) rot=(0.57735,0.57735,0.57735;2.0944rad)
  Profile = -> Sketch006
  ReferenceAxis = -> DatumLine
  Refine = true
  Reversed = true
  Suppress = false
  _ProfileBasedVersion = 1
FEATURE [PartDesign::Chamfer] Chamfer
  AddSubType = 0
  Angle = 45
  Base = -> Groove [Edge25,Edge26]
  BaseFeature = -> Groove
  ChamferType = 0
  FlipDirection = false
  NewSolid = false
  Placement = pos=(0,0,0) rot=(0.57735,0.57735,0.57735;2.0944rad)
  Refine = true
  Size = 1
  Size2 = 1
  SupportTransform = false
  Suppress = false
FEATURE [PartDesign::Fillet] Fillet007
  AddSubType = 0
  Base = -> Chamfer [Edge15,Edge29]
  BaseFeature = -> Chamfer
  NewSolid = false
  Placement = pos=(0,0,0) rot=(0.57735,0.57735,0.57735;2.0944rad)
  Radius = 4
  Refine = true
  SupportTransform = false
  Suppress = false
FEATURE [Sketcher::SketchObject] Sketch007
  ExternalGeometry = -> [Fillet007]
  FullyConstrained = true
  MapMode = 5
  Placement = pos=(-5.6e-15,0,0) rot=(0.57735,0.57735,0.57735;2.0944rad)
  Support = -> [Fillet007]
  sketch-geometry (4):
    g0: Circle CenterX=-119.5 CenterY=20.6148 CenterZ=0 NormalX=0 NormalY=0 NormalZ=1 AngleXU=0 Radius=2.1
    g1: Circle CenterX=-119.5 CenterY=5 CenterZ=0 NormalX=0 NormalY=0 NormalZ=1 AngleXU=0 Radius=2.1
    g2: Circle CenterX=-80.5 CenterY=5 CenterZ=0 NormalX=0 NormalY=0 NormalZ=1 AngleXU=0 Radius=2.1
    g3: Circle CenterX=-80.5 CenterY=36.2148 CenterZ=0 NormalX=0 NormalY=0 NormalZ=1 AngleXU=0 Radius=2.1
  constraints (8):
    c: Coincident(g0,g-3)
    c: Coincident(g1,g-4)
    c: Coincident(g2,g-5)
    c: Coincident(g3,g-6)
    c: Diameter(g3) = 4.2
    c: Equal(g3,g0)
    c: Equal(g3,g1)
    c: Equal(g3,g2)
FEATURE [PartDesign::Pocket] Pocket
  AddSubType = 1
  BaseFeature = -> Fillet007
  CheckUpToFaceLimits = true
  ClaimChildren = false
  Fit = 0
  FitJoin = 0
  InnerFit = 0
  InnerFitJoin = 0
  InnerTaperAngle = 0
  InnerTaperAngleRev = 0
  Length = 5
  Length2 = 100
  Linearize = true
  NewSolid = false
  Placement = pos=(0,0,0) rot=(0.57735,0.57735,0.57735;2.0944rad)
  Profile = -> Sketch007
  Refine = true
  Suppress = false
  Type = 1
  _ProfileBasedVersion = 1
  _Version = 1
FEATURE [PartDesign::Body] Body005  label="MorsDroit"
  AutoGroupSolids = false
  ExportMode = 0
  Group = -> [Binder001,Sketch005,Import,Pad005,Sketch006,DatumLine,Groove,Chamfer,Fillet007,Sketch007,Pocket]
  Origin = -> Origin005
  SingleSolid = true
  Tip = -> Pocket
  _ExportChildren = -> [Binder001,Import,Pad005,DatumLine,Groove,Chamfer,Fillet007,Pocket]
  _GroupVersion = 1
COMPONENT P6 — recipe-attached ("MorsGauche", modeled in this document).
Construction recipe (the document's own serialized feature program — sketch geometry with constraints, then the solid features built on it; lengths are millimeters unless a unit is written):

FEATURE [PartDesign::FeatureBase] BaseFeature
  BaseFeature = -> Part__Mirroring
  NewSolid = false
  Suppress = false
FEATURE [Sketcher::SketchObject] Sketch008
  ExternalGeometry = -> [BaseFeature]
  FullyConstrained = true
  MapMode = 5
  Placement = pos=(-1.008e-13,0,0) rot=(0.57735,-0.57735,-0.57735;2.0944rad)
  Support = -> [BaseFeature]
  sketch-geometry (4):
    g0: Circle CenterX=80.5 CenterY=36.2148 CenterZ=0 NormalX=0 NormalY=0 NormalZ=1 AngleXU=0 Radius=1.6
    g1: Circle CenterX=80.5 CenterY=5 CenterZ=0 NormalX=0 NormalY=0 NormalZ=1 AngleXU=0 Radius=1.6
    g2: Circle CenterX=119.5 CenterY=5 CenterZ=0 NormalX=0 NormalY=0 NormalZ=1 AngleXU=0 Radius=1.6
    g3: Circle CenterX=119.5 CenterY=20.6148 CenterZ=0 NormalX=0 NormalY=0 NormalZ=1 AngleXU=0 Radius=1.6
  constraints (8):
    c: Coincident(g0,g-3)
    c: Coincident(g1,g-4)
    c: Coincident(g2,g-5)
    c: Coincident(g3,g-6)
    c: Diameter(g3) = 3.2
    c: Equal(g3,g2)
    c: Equal(g3,g1)
    c: Equal(g3,g0)
FEATURE [PartDesign::Pad] Pad006
  AddSubType = 0
  BaseFeature = -> BaseFeature
  CheckUpToFaceLimits = true
  ClaimChildren = false
  Direction = (1,1,1)
  Fit = 0
  FitJoin = 0
  InnerFit = 0
  InnerFitJoin = 0
  InnerTaperAngle = 0
  InnerTaperAngleRev = 0
  Length = 10
  Length2 = 100
  Linearize = true
  NewSolid = false
  Profile = -> Sketch008
  Refine = true
  Reversed = true
  Suppress = false
  Type = 3
  UpToFace = -> BaseFeature [Face2]
  _ProfileBasedVersion = 1
FEATURE [PartDesign::Body] Body006  label="MorsGauche"
  AutoGroupSolids = false
  BaseFeature = -> Part__Mirroring
  ExportMode = 0
  Group = -> [BaseFeature,Sketch008,Pad006]
  Origin = -> Origin006
  SingleSolid = true
  Tip = -> Pad006
  _ExportChildren = -> [BaseFeature,Pad006]
  _GroupVersion = 1
COMPONENT P7 — recipe-attached ("608ZZ", modeled in this document).
Construction recipe (the document's own serialized feature program — sketch geometry with constraints, then the solid features built on it; lengths are millimeters unless a unit is written):

FEATURE [Sketcher::SketchObject] Sketch009
  FullyConstrained = true
  MapMode = 5
  Placement = pos=(0,0,0) rot=(1,0,0;1.5708rad)
  Support = -> [XZ_Plane007]
  sketch-geometry (12):
    g0: LineSegment StartX=0 StartY=11 StartZ=0 EndX=7 EndY=11 EndZ=0
    g1: LineSegment StartX=7 StartY=11 StartZ=0 EndX=7 EndY=9.5 EndZ=0
    g2: LineSegment StartX=7 StartY=9.5 StartZ=0 EndX=6.8 EndY=9.5 EndZ=0
    g3: LineSegment StartX=0 StartY=9.5 StartZ=0 EndX=0 EndY=11 EndZ=0
    g4: LineSegment StartX=0 StartY=5.5 StartZ=0 EndX=0.2 EndY=5.5 EndZ=0
    g5: LineSegment StartX=7 StartY=5.5 StartZ=0 EndX=7 EndY=4 EndZ=0
    g6: LineSegment StartX=7 StartY=4 StartZ=0 EndX=0 EndY=4 EndZ=0
    g7: LineSegment StartX=0 StartY=4 StartZ=0 EndX=0 EndY=5.5 EndZ=0
    g8: LineSegment StartX=6.8 StartY=9.5 StartZ=0 EndX=6.8 EndY=5.5 EndZ=0
    g9: LineSegment StartX=0.2 StartY=5.5 StartZ=0 EndX=0.2 EndY=9.5 EndZ=0
    g10: LineSegment StartX=0.2 StartY=9.5 StartZ=0 EndX=0 EndY=9.5 EndZ=0
    g11: LineSegment StartX=6.8 StartY=5.5 StartZ=0 EndX=7 EndY=5.5 EndZ=0
  constraints (34):
    c: Coincident(g0,g1)
    c: Coincident(g1,g2)
    c: Coincident(g10,g3)
    c: Coincident(g3,g0)
    c: Horizontal(g0)
    c: Horizontal(g2)
    c: Vertical(g1)
    c: Vertical(g3)
    c: PointOnObject(g0,g-2)
    c: Coincident(g11,g5)
    c: Coincident(g5,g6)
    c: Coincident(g6,g7)
    c: Coincident(g7,g4)
    c: Horizontal(g4)
    c: Horizontal(g6)
    c: Vertical(g5)
    c: Vertical(g7)
    c: PointOnObject(g4,g-2)
    c: Vertical(g8)
    c: Vertical(g9)
    c: Tangent(g2,g10)
    c: Coincident(g11,g8)
    c: Tangent(g4,g11)
    c: Coincident(g9,g10)
    c: Coincident(g9,g4)
    c: Coincident(g8,g2)
    c: PointOnObject(g1,g5)
    c: Equal(g2,g10)
    c: DistanceY(g6) = 4
    c: DistanceY(g0) = 11
    c: DistanceY(g3,g3) = 1.5
    c: DistanceY(g7,g7) = 1.5
    c: DistanceX(g10,g10) = 0.2
    c: DistanceX(g0,g0) = 7
FEATURE [PartDesign::Revolution] Revolution
  AddSubType = 0
  Angle = 360
  Axis = (1,0,0)
  Base = (0,0,0)
  ClaimChildren = false
  Fit = 0
  FitJoin = 0
  InnerFit = 0
  InnerFitJoin = 0
  NewSolid = false
  Placement = pos=(0,0,0) rot=(1,0,0;1.5708rad)
  Profile = -> Sketch009
  ReferenceAxis = -> Sketch009 [H_Axis]
  Refine = true
  Suppress = false
  _ProfileBasedVersion = 1
FEATURE [PartDesign::Chamfer] Chamfer001
  AddSubType = 0
  Angle = 45
  Base = -> Revolution [Edge1,Edge2,Edge10,Edge11]
  BaseFeature = -> Revolution
  ChamferType = 0
  FlipDirection = false
  NewSolid = false
  Placement = pos=(0,0,0) rot=(1,0,0;1.5708rad)
  Refine = true
  Size = 0.2
  Size2 = 1
  SupportTransform = false
  Suppress = false
FEATURE [PartDesign::Body] Body007  label="608ZZ"
  AutoGroupSolids = false
  ExportMode = 0
  Group = -> [Sketch009,Revolution,Chamfer001]
  Origin = -> Origin009
  SingleSolid = true
  Tip = -> Chamfer001
  _ExportChildren = -> [Revolution,Chamfer001]
  _GroupVersion = 1
COMPONENT P8 — recipe-attached ("Profil20x40", modeled in this document).
Construction recipe (the document's own serialized feature program — sketch geometry with constraints, then the solid features built on it; lengths are millimeters unless a unit is written):

FEATURE [Sketcher::SketchObject] Sketch010
  FullyConstrained = true
  MapMode = 5
  Support = -> [XY_Plane008]
  sketch-geometry (61):
    g0: Circle CenterX=-10 CenterY=0 CenterZ=0 NormalX=0 NormalY=0 NormalZ=1 AngleXU=0 Radius=2.5
    g1: Circle CenterX=10 CenterY=0 CenterZ=0 NormalX=0 NormalY=0 NormalZ=1 AngleXU=0 Radius=2.5
    g2: LineSegment StartX=-12.9393 StartY=4 StartZ=0 EndX=-7.06066 EndY=4 EndZ=0
    g3: LineSegment StartX=-7.06066 StartY=4 StartZ=0 EndX=-3.06066 EndY=8 EndZ=0
    g4: LineSegment StartX=-3.06066 StartY=8 StartZ=0 EndX=-6.9 EndY=8 EndZ=0
    g5: LineSegment StartX=-6.9 StartY=8 StartZ=0 EndX=-6.9 EndY=10 EndZ=0
    g6: LineSegment StartX=-6.9 StartY=10 StartZ=0 EndX=6.9 EndY=10 EndZ=0
    g7: LineSegment StartX=6.9 StartY=10 StartZ=0 EndX=6.9 EndY=8 EndZ=0
    g8: LineSegment StartX=6.9 StartY=8 StartZ=0 EndX=3.06066 EndY=8 EndZ=0
    g9: LineSegment StartX=3.06066 StartY=8 StartZ=0 EndX=7.06066 EndY=4 EndZ=0
    g10: LineSegment StartX=7.06066 StartY=4 StartZ=0 EndX=12.9393 EndY=4 EndZ=0
    g11: LineSegment StartX=12.9393 StartY=4 StartZ=0 EndX=16.9393 EndY=8 EndZ=0
    g12: LineSegment StartX=16.9393 StartY=8 StartZ=0 EndX=13.1 EndY=8 EndZ=0
    g13: LineSegment StartX=13.1 StartY=8 StartZ=0 EndX=13.1 EndY=10 EndZ=0
    g14: LineSegment StartX=13.1 StartY=10 StartZ=0 EndX=20 EndY=10 EndZ=0
    g15: LineSegment StartX=20 StartY=10 StartZ=0 EndX=20 EndY=3.1 EndZ=0
    g16: LineSegment StartX=20 StartY=3.1 StartZ=0 EndX=18 EndY=3.1 EndZ=0
    g17: LineSegment StartX=18 StartY=3.1 StartZ=0 EndX=18 EndY=6.93934 EndZ=0
    g18: LineSegment StartX=18 StartY=6.93934 StartZ=0 EndX=14 EndY=2.93934 EndZ=0
    g19: LineSegment StartX=14 StartY=2.93934 StartZ=0 EndX=14 EndY=-2.93934 EndZ=0
    g20: LineSegment StartX=14 StartY=-2.93934 StartZ=0 EndX=18 EndY=-6.93934 EndZ=0
    g21: LineSegment StartX=18 StartY=-6.93934 StartZ=0 EndX=18 EndY=-3.1 EndZ=0
    g22: LineSegment StartX=18 StartY=-3.1 StartZ=0 EndX=20 EndY=-3.1 EndZ=0
    g23: LineSegment StartX=20 StartY=-3.1 StartZ=0 EndX=20 EndY=-10 EndZ=0
    g24: LineSegment StartX=20 StartY=-10 StartZ=0 EndX=13.1 EndY=-10 EndZ=0
    g25: LineSegment StartX=13.1 StartY=-10 StartZ=0 EndX=13.1 EndY=-8 EndZ=0
    g26: LineSegment StartX=13.1 StartY=-8 StartZ=0 EndX=16.9393 EndY=-8 EndZ=0
    g27: LineSegment StartX=16.9393 StartY=-8 StartZ=0 EndX=12.9393 EndY=-4 EndZ=0
    g28: LineSegment StartX=12.9393 StartY=-4 StartZ=0 EndX=7.06066 EndY=-4 EndZ=0
    g29: LineSegment StartX=7.06066 StartY=-4 StartZ=0 EndX=3.06066 EndY=-8 EndZ=0
    g30: LineSegment StartX=3.06066 StartY=-8 StartZ=0 EndX=6.9 EndY=-8 EndZ=0
    g31: LineSegment StartX=6.9 StartY=-8 StartZ=0 EndX=6.9 EndY=-10 EndZ=0
    g32: LineSegment StartX=6.9 StartY=-10 StartZ=0 EndX=-6.9 EndY=-10 EndZ=0
    g33: LineSegment StartX=-6.9 StartY=-10 StartZ=0 EndX=-6.9 EndY=-8 EndZ=0
    g34: LineSegment StartX=-6.9 StartY=-8 StartZ=0 EndX=-3.06066 EndY=-8 EndZ=0
    g35: LineSegment StartX=-3.06066 StartY=-8 StartZ=0 EndX=-7.06066 EndY=-4 EndZ=0
    g36: LineSegment StartX=-7.06066 StartY=-4 StartZ=0 EndX=-12.9393 EndY=-4 EndZ=0
    g37: LineSegment StartX=-12.9393 StartY=-4 StartZ=0 EndX=-16.9393 EndY=-8 EndZ=0
    g38: LineSegment StartX=-16.9393 StartY=-8 StartZ=0 EndX=-13.1 EndY=-8 EndZ=0
    g39: LineSegment StartX=-13.1 StartY=-8 StartZ=0 EndX=-13.1 EndY=-10 EndZ=0
    g40: LineSegment StartX=-13.1 StartY=-10 StartZ=0 EndX=-20 EndY=-10 EndZ=0
    g41: LineSegment StartX=-20 StartY=-10 StartZ=0 EndX=-20 EndY=-3.1 EndZ=0
    g42: LineSegment StartX=-20 StartY=-3.1 StartZ=0 EndX=-18 EndY=-3.1 EndZ=0
    g43: LineSegment StartX=-18 StartY=-3.1 StartZ=0 EndX=-18 EndY=-6.93934 EndZ=0
    g44: LineSegment StartX=-18 StartY=-6.93934 StartZ=0 EndX=-14 EndY=-2.93934 EndZ=0
    g45: LineSegment StartX=-14 StartY=-2.93934 StartZ=0 EndX=-14 EndY=2.93934 EndZ=0
    g46: LineSegment StartX=-14 StartY=2.93934 StartZ=0 EndX=-18 EndY=6.93934 EndZ=0
    g47: LineSegment StartX=-18 StartY=6.93934 StartZ=0 EndX=-18 EndY=3.1 EndZ=0
    g48: LineSegment StartX=-18 StartY=3.1 StartZ=0 EndX=-20 EndY=3.1 EndZ=0
    g49: LineSegment StartX=-20 StartY=3.1 StartZ=0 EndX=-20 EndY=10 EndZ=0
    g50: LineSegment StartX=-20 StartY=10 StartZ=0 EndX=-13.1 EndY=10 EndZ=0
    g51: LineSegment StartX=-13.1 StartY=10 StartZ=0 EndX=-13.1 EndY=8 EndZ=0
    g52: LineSegment StartX=-13.1 StartY=8 StartZ=0 EndX=-16.9393 EndY=8 EndZ=0
    g53: LineSegment StartX=-16.9393 StartY=8 StartZ=0 EndX=-12.9393 EndY=4 EndZ=0
    g54: LineSegment [constr] StartX=-10 StartY=-10 StartZ=0 EndX=-10 EndY=10 EndZ=0
    g55: LineSegment StartX=-6 StartY=-2.93934 StartZ=0 EndX=-6 EndY=2.93934 EndZ=0
    g56: LineSegment StartX=-6 StartY=2.93934 StartZ=0 EndX=0 EndY=8.93934 EndZ=0
    g57: LineSegment StartX=0 StartY=8.93934 StartZ=0 EndX=6 EndY=2.93934 EndZ=0
    g58: LineSegment StartX=6 StartY=2.93934 StartZ=0 EndX=6 EndY=-2.93934 EndZ=0
    g59: LineSegment StartX=6 StartY=-2.93934 StartZ=0 EndX=0 EndY=-8.93934 EndZ=0
    g60: LineSegment StartX=0 StartY=-8.93934 StartZ=0 EndX=-6 EndY=-2.93934 EndZ=0
  constraints (166):
    c: PointOnObject(g0,g-1)
    c: Symmetric(g1,g0,g-1)
    c: Diameter(g0) = 5
    c: Equal(g0,g1)
    c: DistanceX(g0,g1) = 20
    c: Horizontal(g2)
    c: Coincident(g2,g3)
    c: Coincident(g3,g4)
    c: Horizontal(g4)
    c: Coincident(g4,g5)
    c: Vertical(g5)
    c: Coincident(g5,g6)
    c: Coincident(g6,g7)
    c: Vertical(g7)
    c: Coincident(g7,g8)
    c: Horizontal(g8)
    c: Coincident(g8,g9)
    c: Coincident(g9,g10)
    c: Horizontal(g10)
    c: Coincident(g10,g11)
    c: Coincident(g11,g12)
    c: Horizontal(g12)
    c: Coincident(g12,g13)
    c: Vertical(g13)
    c: Coincident(g13,g14)
    c: Horizontal(g14)
    c: Coincident(g14,g15)
    c: Vertical(g15)
    c: Coincident(g15,g16)
    c: Coincident(g16,g17)
    c: Vertical(g17)
    c: Coincident(g17,g18)
    c: Coincident(g18,g19)
    c: Coincident(g19,g20)
    c: Coincident(g20,g21)
    c: Vertical(g21)
    c: Coincident(g21,g22)
    c: Horizontal(g22)
    c: Coincident(g22,g23)
    c: Vertical(g23)
    c: Coincident(g23,g24)
    c: Horizontal(g24)
    c: Coincident(g24,g25)
    c: Coincident(g25,g26)
    c: Horizontal(g26)
    c: Coincident(g26,g27)
    c: Coincident(g27,g28)
    c: Horizontal(g28)
    c: Coincident(g28,g29)
    c: Coincident(g29,g30)
    c: Horizontal(g30)
    c: Coincident(g30,g31)
    c: Vertical(g31)
    c: Coincident(g31,g32)
    c: Coincident(g32,g33)
    c: Vertical(g33)
    c: Coincident(g33,g34)
    c: Horizontal(g34)
    c: Coincident(g34,g35)
    c: Coincident(g35,g36)
    c: Coincident(g36,g37)
    c: Coincident(g37,g38)
    c: Horizontal(g38)
    c: Coincident(g38,g39)
    c: Vertical(g39)
    c: Coincident(g39,g40)
    c: Horizontal(g40)
    c: Coincident(g40,g41)
    c: Vertical(g41)
    c: Coincident(g41,g42)
    c: Horizontal(g42)
    c: Coincident(g42,g43)
    c: Vertical(g43)
    c: Coincident(g43,g44)
    c: Coincident(g44,g45)
    c: Coincident(g45,g46)
    c: Coincident(g46,g47)
    c: Vertical(g47)
    c: Coincident(g47,g48)
    c: Coincident(g48,g49)
    c: Vertical(g49)
    c: Coincident(g49,g50)
    c: Horizontal(g50)
    c: Coincident(g50,g51)
    c: Vertical(g51)
    c: Coincident(g51,g52)
    c: Horizontal(g52)
    c: Coincident(g52,g53)
    c: Coincident(g53,g2)
    c: Horizontal(g48)
    c: Horizontal(g16)
    c: Symmetric(g5,g6,g-2)
    c: Symmetric(g3,g8,g-2)
    c: Symmetric(g9,g2,g-2)
    c: Symmetric(g35,g28,g-2)
    c: Symmetric(g34,g29,g-2)
    c: Symmetric(g32,g31,g-2)
    c: Symmetric(g34,g3,g-1)
    c: Symmetric(g35,g2,g-1)
    c: Angle(g3,g2) = 2.35619
    c: Symmetric(g5,g32,g-1)
    c: PointOnObject(g50,g6)
    c: Symmetric(g49,g14,g-2)
    c: Symmetric(g49,g40,g-1)
    c: Symmetric(g40,g23,g-2)
    c: Equal(g3,g53)
    c: Equal(g53,g46)
    c: Equal(g46,g44)
    c: Parallel(g46,g53)
    c: Parallel(g44,g37)
    c: Parallel(g18,g11)
    c: Parallel(g20,g27)
    c: DistanceY(g40,g49) = 20
    c: DistanceX(g49,g14) = 40
    c: DistanceX(g50,g5) = 6.2
    c: Equal(g49,g50)
    c: Equal(g41,g49)
    c: Equal(g40,g24)
    c: Equal(g40,g41)
    c: Vertical(g25)
    c: Equal(g25,g31)
    c: Equal(g39,g33)
    c: Equal(g39,g42)
    c: Equal(g42,g48)
    c: Equal(g48,g51)
    c: DistanceY(g24,g27) = 6
    c: Equal(g30,g26)
    c: Equal(g21,g17)
    c: PointOnObject(g21,g17)
    c: Equal(g12,g8)
    c: PointOnObject(g12,g8)
    c: Equal(g4,g52)
    c: DistanceY(g25,g25) = 2
    c: Equal(g25,g22)
    c: Equal(g14,g15)
    c: Equal(g23,g24)
    c: Equal(g24,g14)
    c: Symmetric(g45,g44,g-1)
    c: Symmetric(g18,g19,g-1)
    c: PointOnObject(g0,g54)
    c: PointOnObject(g54,g6)
    c: PointOnObject(g54,g32)
    c: Symmetric(g2,g2,g54)
    c: Symmetric(g35,g36,g54)
    c: Equal(g2,g45)
    c: Equal(g10,g2)
    c: Equal(g19,g10)
    c: Equal(g17,g12)
    c: Distance(g11,g17) = 1.5
    c: Vertical(g55)
    c: Coincident(g55,g56)
    c: PointOnObject(g56,g-2)
    c: Coincident(g56,g57)
    c: Coincident(g57,g58)
    c: Vertical(g58)
    c: Coincident(g58,g59)
    c: Coincident(g59,g60)
    c: Coincident(g60,g55)
    c: Parallel(g60,g35)
    c: Parallel(g56,g3)
    c: Parallel(g57,g9)
    c: Parallel(g59,g29)
    c: Equal(g58,g55)
    c: Symmetric(g56,g59,g-1)
    c: Equal(g55,g45)
    c: Distance(g57,g9) = 1.5
FEATURE [PartDesign::Pad] Pad007
  AddSubType = 0
  CheckUpToFaceLimits = true
  ClaimChildren = false
  Direction = (1,1,1)
  Fit = 0
  FitJoin = 0
  InnerFit = 0
  InnerFitJoin = 0
  InnerTaperAngle = 0
  InnerTaperAngleRev = 0
  Length = 300
  Length2 = 100
  Linearize = true
  NewSolid = false
  Profile = -> Sketch010
  Refine = true
  Suppress = false
  Type = 0
  _ProfileBasedVersion = 1
FEATURE [PartDesign::Fillet] Fillet008
  AddSubType = 0
  Base = -> Pad007 [Edge161,Edge170]
  BaseFeature = -> Pad007
  NewSolid = false
  Radius = 2
  Refine = true
  SupportTransform = false
  Suppress = false
FEATURE [PartDesign::Fillet] Fillet009
  AddSubType = 0
  Base = -> Fillet008 [Edge178,Edge184,Edge135,Edge3,Edge134,Edge133,Edge177,Edge169,Edge175,Edge166,Edge161,Edge160,Edge159,Edge168,Edge167,Edge140,Edge143,Edge149,Edge152,Edge158,Edge129,Edge131,Edge68]
  BaseFeature = -> Fillet008
  NewSolid = false
  Radius = 0.4
  Refine = true
  SupportTransform = false
  Suppress = false
FEATURE [PartDesign::Fillet] Fillet010
  AddSubType = 0
  Base = -> Fillet009 [Edge240,Edge218,Edge197,Edge221]
  BaseFeature = -> Fillet009
  NewSolid = false
  Radius = 0.5
  Refine = true
  SupportTransform = false
  Suppress = false
FEATURE [PartDesign::Chamfer] Chamfer002
  AddSubType = 0
  Angle = 45
  Base = -> Fillet010 [Edge187,Edge223,Edge175,Edge139,Edge135,Edge91,Edge97,Edge137,Edge149,Edge193,Edge197,Edge235]
  BaseFeature = -> Fillet010
  ChamferType = 0
  FlipDirection = false
  NewSolid = false
  Refine = true
  Size = 1
  Size2 = 1
  SupportTransform = false
  Suppress = false
FEATURE [PartDesign::Body] Body008  label="Profil20x40"
  AutoGroupSolids = false
  ExportMode = 0
  Group = -> [Sketch010,Pad007,Fillet008,Fillet009,Fillet010,Chamfer002]
  Origin = -> Origin011
  SingleSolid = true
  Tip = -> Chamfer002
  _ExportChildren = -> [Pad007,Fillet008,Fillet009,Fillet010,Chamfer002]
  _GroupVersion = 1
COMPONENT P9 — geometry summary ("Presse"; no construction recipe available for this part):
  bounding box: 329.0 x 159.1 x 68.0 mm
  tessellated surface: 412,540 triangles
  volume: 291976 mm^3 (8% of its bounding box)
PROVENANCE & LICENSES
A FreeCAD (.FCStd) document from a public repository crawl; recipes are the document's own serialized feature recipes (and, for linked parts, companion documents' recipes).
License: mit.
